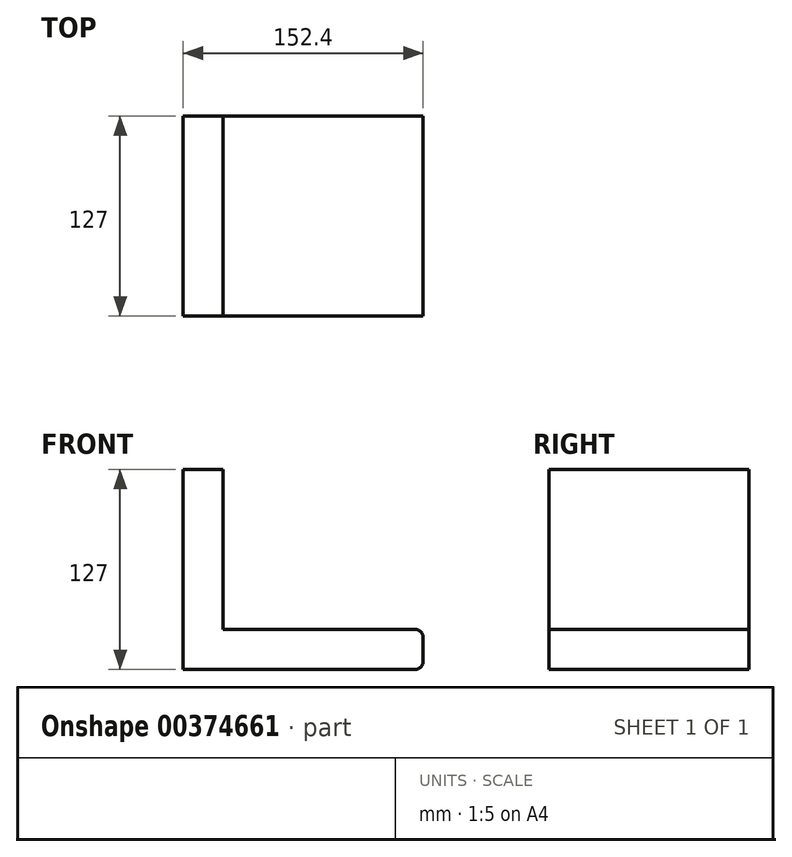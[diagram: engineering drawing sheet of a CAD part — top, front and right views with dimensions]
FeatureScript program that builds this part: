
annotation { "Feature Type Name" : "Feature", "Feature Type Description" : "" }
export const myFeature = defineFeature(function(context is Context, id is Id, definition is map)
    precondition{}
    {
        {
            var Q0;
            Q0=qCreatedBy(makeId("Front.planeOp"),FACE);
            var sketch = newSketch(context, id + "F0", { "sketchPlane" : qUnion([Q0])});
            skLineSegment(sketch, "E0", {"start": v(0, 0) * mm, "end": v(0, 127) * mm});
            skLineSegment(sketch, "E1", {"start": v(0, 127) * mm, "end": v(25.4, 127) * mm});
            skLineSegment(sketch, "E2", {"start": v(25.4, 127) * mm, "end": v(25.4, 25.4) * mm});
            skLineSegment(sketch, "E3", {"start": v(25.4, 25.4) * mm, "end": v(152.4, 25.4) * mm});
            skLineSegment(sketch, "E4", {"start": v(152.4, 25.4) * mm, "end": v(152.4, 0) * mm});
            skLineSegment(sketch, "E5", {"start": v(152.4, 0) * mm, "end": v(0, 0) * mm});
            skSolve(sketch);
        }
        {
            var Q0;
            Q0 = qSketchRegion(id + "F0", true);
            extrude(context, id + "F1", {"entities" : qUnion([Q0]), "depth" : 127 * mm});
        }
        {
            var Q0;
            Q0=makeQuery(id+"F1.opExtrude","SWEPT_EDGE",EDGE,{"disambiguationData":[OSD([sQuery(id+"F0.wireOp",EDGE,"E4"),sQuery(id+"F0.wireOp",EDGE,"E5")])]});
            var Q1;
            Q1=makeQuery(id+"F1.opExtrude","SWEPT_EDGE",EDGE,{"disambiguationData":[OSD([sQuery(id+"F0.wireOp",EDGE,"E3"),sQuery(id+"F0.wireOp",EDGE,"E4")])]});
            fillet(context, id + "F2", {"entities" : qUnion([Q0, Q1]), "radius" : 5.08 * mm, "tangentPropagation" : true, "allowEdgeOverflow" : false});
        }
    });
